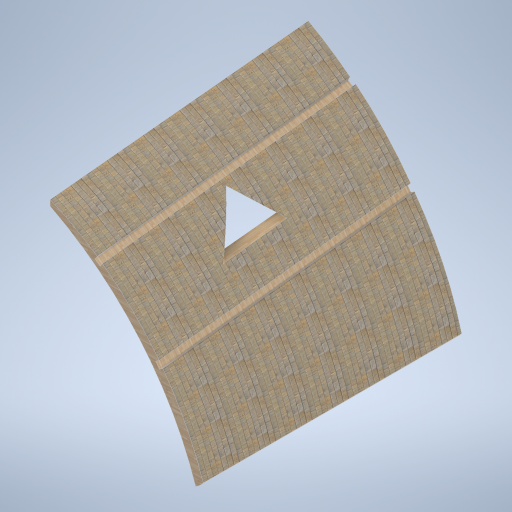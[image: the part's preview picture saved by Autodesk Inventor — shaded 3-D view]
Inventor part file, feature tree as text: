
AUTODESK INVENTOR PART (.ipt)
format: ipt  version: 2024.2 (Build 282272000, 272)  size: 534,528 bytes
history: native  units: mm
features: sketch x3, plane x3, loft x1, extrude x1
ambient origin geometry x8: Origin, YZ Plane, XZ Plane, XY Plane, X Axis, Y Axis, Z Axis, Center Point
bodies: Solid1 (feature_tree)
feature tree (8):
  sketch  "Sketch1"  dims[d5=0.0mm d6=-7900.0mm d7=800.0mm]
  plane  "Work Plane2"
  loft  "Loft1"
  plane  "Work Plane3"
  extrude  "Extrusion1"  Depth=9000.0mm
  plane  "Work Plane1"
  sketch  "Sketch2"  dims[d8=9000.0mm d9=9000.0mm]
  sketch  "Sketch3"  dims[d10=9000.0mm d11=9000.0mm d12=800.0mm d13=0.0mm d14=90.0deg d15=0.0mm d16=90.0deg d17=2500.0mm d18=0.0mm d19=0.0mm]
